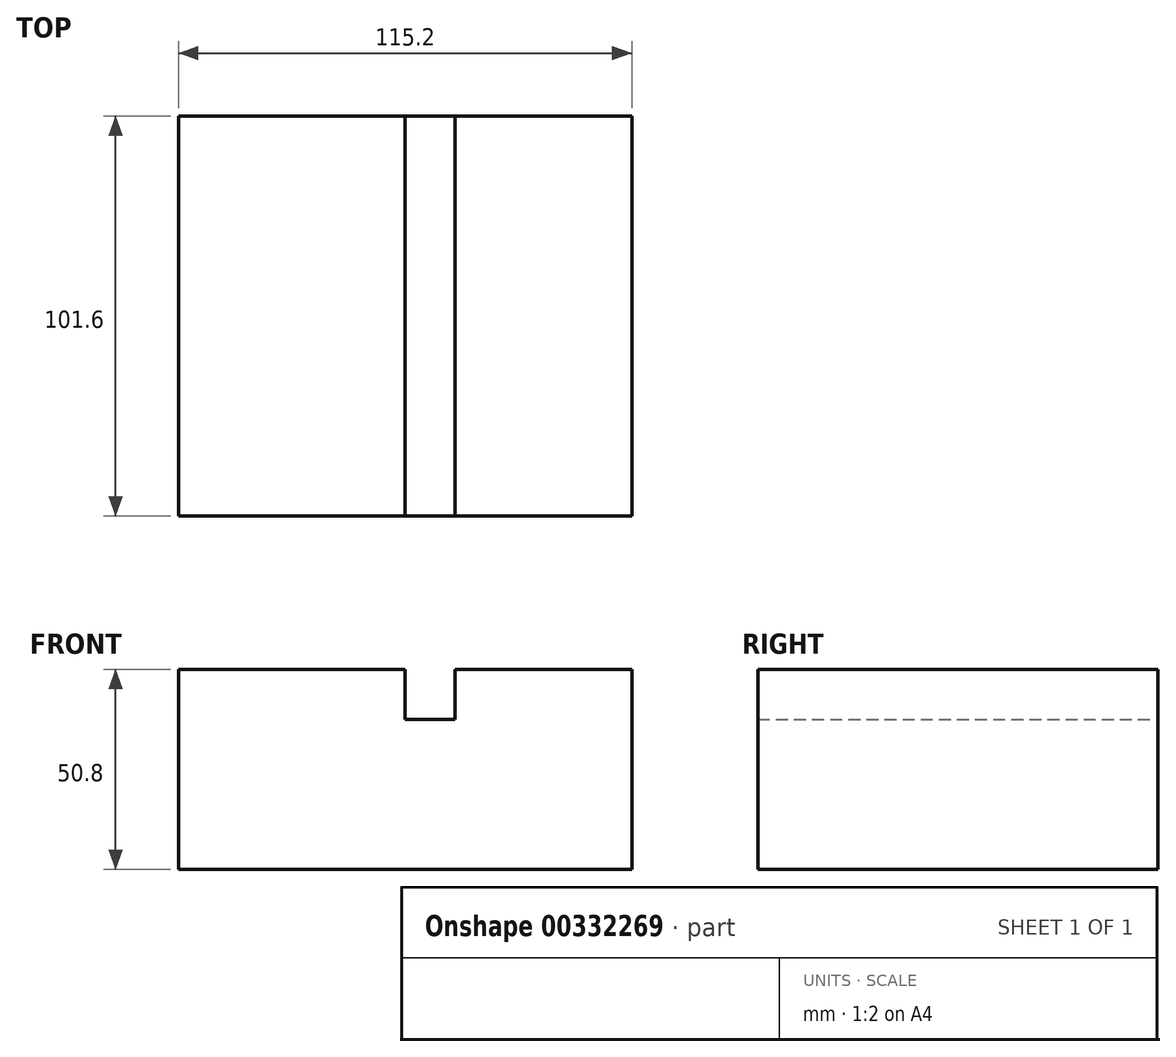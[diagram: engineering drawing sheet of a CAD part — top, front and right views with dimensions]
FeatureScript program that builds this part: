
annotation { "Feature Type Name" : "Feature", "Feature Type Description" : "" }
export const myFeature = defineFeature(function(context is Context, id is Id, definition is map)
    precondition{}
    {
        {
            var Q0;
            Q0=qCreatedBy(makeId("Front.planeOp"),FACE);
            var sketch = newSketch(context, id + "F0", { "sketchPlane" : qUnion([Q0])});
            skLineSegment(sketch, "E0.top", {"start": v(-70.3, -43.21) * mm, "end": v(44.9, -43.21) * mm});
            skLineSegment(sketch, "E0.right", {"start": v(44.9, 7.59) * mm, "end": v(44.9, -43.21) * mm});
            skLineSegment(sketch, "E1", {"start": v(-70.3, 7.59) * mm, "end": v(-70.3, -43.21) * mm});
            skLineSegment(sketch, "E2", {"start": v(-12.7, 7.59) * mm, "end": v(-12.7, -5.11) * mm});
            skLineSegment(sketch, "E3", {"start": v(-12.7, -5.11) * mm, "end": v(0, -5.11) * mm});
            skLineSegment(sketch, "E4", {"start": v(-70.3, 7.59) * mm, "end": v(-12.7, 7.59) * mm});
            skLineSegment(sketch, "E5", {"start": v(0, 7.59) * mm, "end": v(44.9, 7.59) * mm});
            skLineSegment(sketch, "E6", {"start": v(0, -5.11) * mm, "end": v(0, 7.59) * mm});
            skSolve(sketch);
        }
        {
            var Q0;
            Q0=makeQuery(id+"F0.imprint","IMPRINT",FACE,{"disambiguationData":[TD([[makeQuery(id+"F0.imprint","IMPRINT",EDGE,{"derivedFrom":sQuery(id+"F0.wireOp",EDGE,"E0.top")}),1.0]])]});
            extrude(context, id + "F1", {"entities" : qUnion([Q0]), "depth" : 101.6 * mm});
        }
    });
